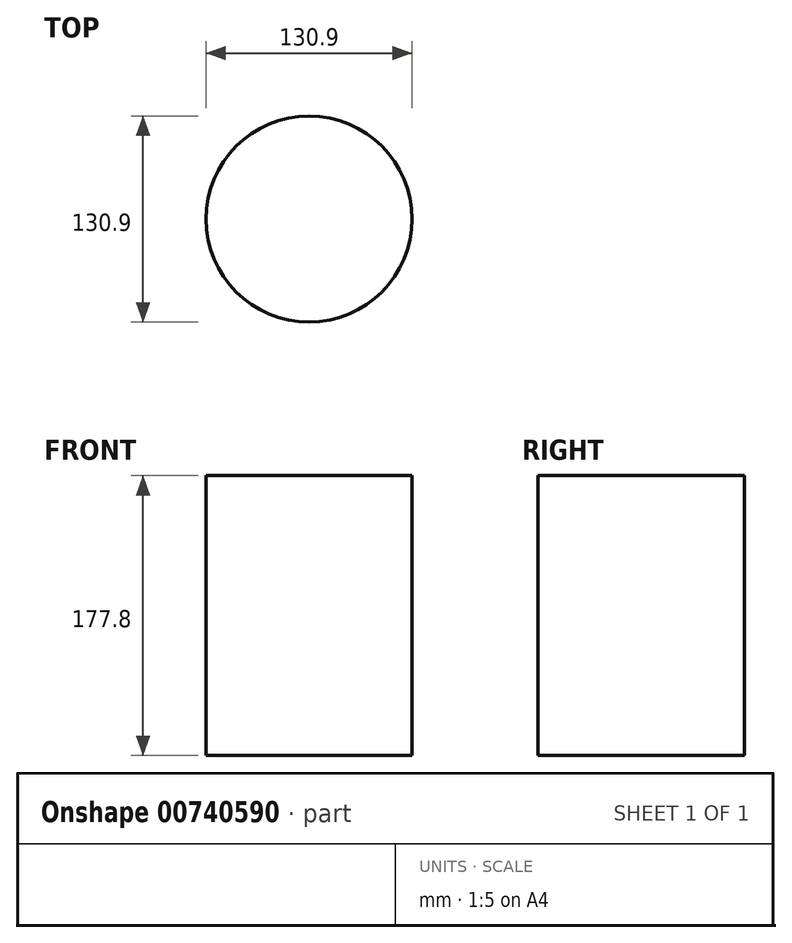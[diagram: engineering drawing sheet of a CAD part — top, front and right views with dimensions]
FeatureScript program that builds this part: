
annotation { "Feature Type Name" : "Feature", "Feature Type Description" : "" }
export const myFeature = defineFeature(function(context is Context, id is Id, definition is map)
    precondition{}
    {
        {
            var Q0;
            Q0=qCreatedBy(makeId("Top.planeOp"),FACE);
            var sketch = newSketch(context, id + "F0", { "sketchPlane" : qUnion([Q0])});
            skCircle(sketch, "E0", {"center": v(0, 0) * mm, "radius": 65.45 * mm});
            skSolve(sketch);
        }
        {
            var Q0;
            Q0=makeQuery(id+"F0.imprint","IMPRINT",FACE,{"disambiguationData":[TD([[makeQuery(id+"F0.imprint","IMPRINT",EDGE,{"derivedFrom":sQuery(id+"F0.wireOp",EDGE,"E0")}),1.0]])]});
            extrude(context, id + "F1", {"entities" : qUnion([Q0]), "depth" : 177.8 * mm, "offsetDistance" : 25.4 * mm});
        }
    });
